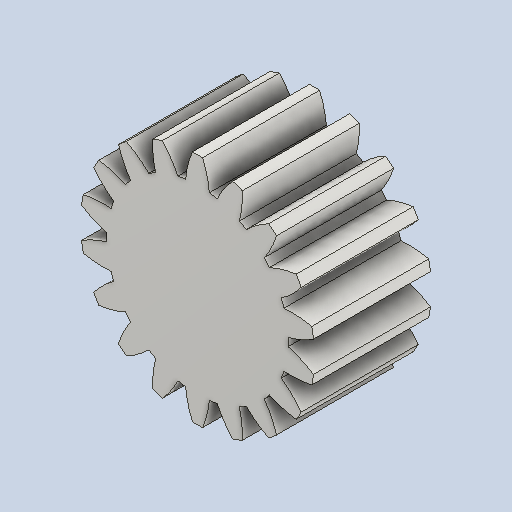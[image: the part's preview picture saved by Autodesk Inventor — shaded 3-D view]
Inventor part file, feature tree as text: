
AUTODESK INVENTOR PART (.ipt)
format: ipt  version: 2023 (Build 270158000, 158)  size: 246,272 bytes
history: native  units: mm (DEFAULTED — no unit token found)
features: plane x3, other x3, sketch x2, extrude x1
ambient origin geometry x8: Origin, YZ Plane, XZ Plane, XY Plane, X Axis, Y Axis, Z Axis, Center Point
bodies: Solid1 (feature_tree)
feature tree (9):
  extrude  "Extrusion1"  Depth=20.0mm TaperAngle=0.0deg
  plane  "Work Plane2"
  plane  "Work Plane8"
  plane  "Work Plane9"
  other  "Spur Gear"
  sketch  "Sketch1"  dims[d0=40.0mm d1=20.0mm d2=0.0mm]
  sketch  "Sketch2"  dims[d3=36.0mm d4=10.0mm d5=0.0mm d16=39.0mm d17=0.0mm d34=1.745329mm d39=0.0mm d41=0.0mm d43=39.0mm d46=39.0mm d47=0.0mm d48=0.0mm]
  other  "Srf1"
  other  "Pitch Diameter"
